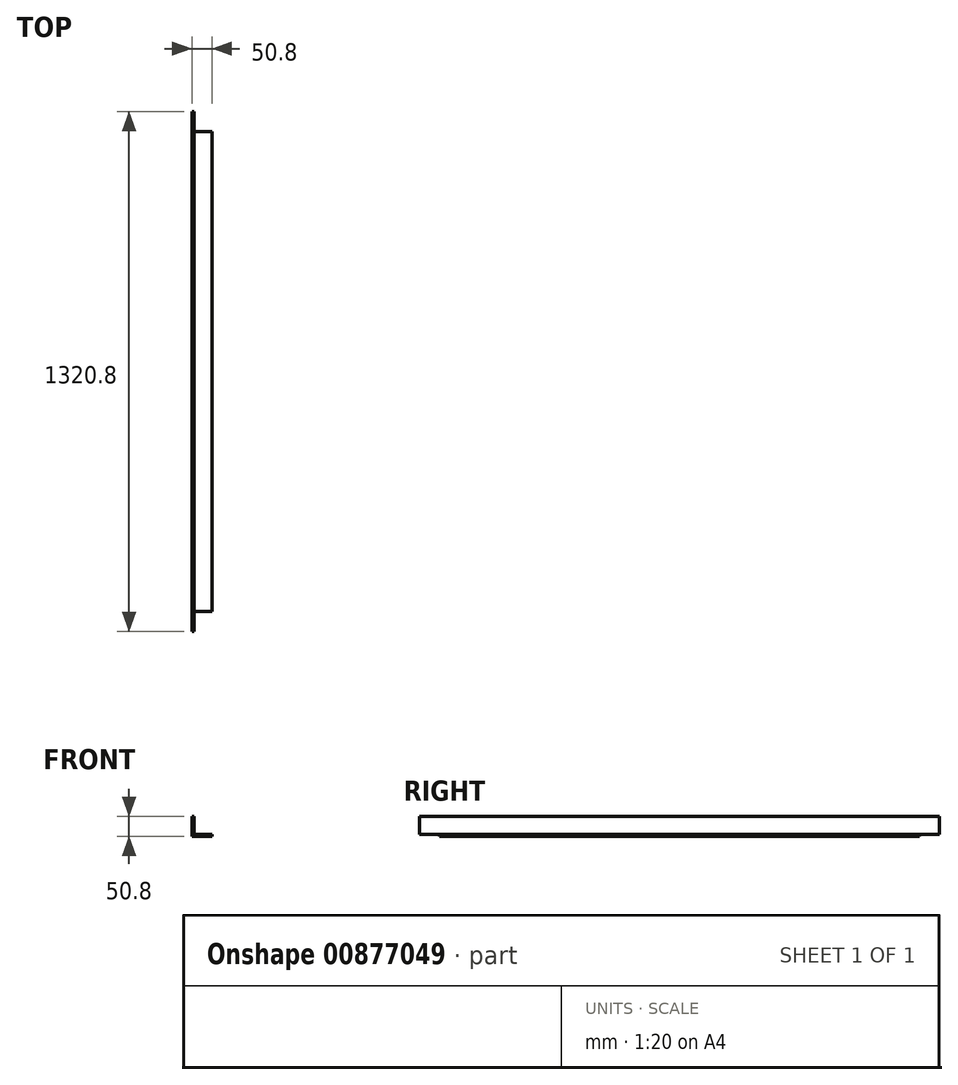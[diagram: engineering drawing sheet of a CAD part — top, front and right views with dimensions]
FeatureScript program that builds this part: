
annotation { "Feature Type Name" : "Feature", "Feature Type Description" : "" }
export const myFeature = defineFeature(function(context is Context, id is Id, definition is map)
    precondition{}
    {
        {
            var Q0;
            Q0=qCreatedBy(makeId("Front.planeOp"),FACE);
            var sketch = newSketch(context, id + "F0", { "sketchPlane" : qUnion([Q0])});
            skLineSegment(sketch, "E0", {"start": v(0, 0) * mm, "end": v(0, 50.8) * mm});
            skLineSegment(sketch, "E1", {"start": v(0, 50.8) * mm, "end": v(4.76, 50.8) * mm});
            skLineSegment(sketch, "E2", {"start": v(4.76, 50.8) * mm, "end": v(4.76, 4.76) * mm});
            skLineSegment(sketch, "E3", {"start": v(4.76, 4.76) * mm, "end": v(50.8, 4.76) * mm});
            skLineSegment(sketch, "E4", {"start": v(50.8, 4.76) * mm, "end": v(50.8, 0) * mm});
            skLineSegment(sketch, "E5", {"start": v(50.8, 0) * mm, "end": v(0, 0) * mm});
            skSolve(sketch);
        }
        {
            var Q0;
            Q0=qSketchRegion(id+"F0",true);
            extrude(context, id + "F1", {"entities" : qUnion([Q0]), "endBound" : BoundingType.SYMMETRIC, "depth" : 1320.8 * mm, "offsetDistance" : 25.4 * mm});
        }
        {
            var Q0;
            Q0=makeQuery(id+"F1.opExtrude","SWEPT_FACE",FACE,{"disambiguationData":[OSD([sQuery(id+"F0.wireOp",EDGE,"E5")])]});
            var sketch = newSketch(context, id + "F2", { "sketchPlane" : qUnion([Q0])});
            skLineSegment(sketch, "E6", {"start": v(50.8, 609.6) * mm, "end": v(50.8, 660.4) * mm});
            skLineSegment(sketch, "E7", {"start": v(50.8, 660.4) * mm, "end": v(0, 660.4) * mm});
            skLineSegment(sketch, "E8", {"start": v(0, 0) * mm, "end": v(50.8, 0) * mm, "construction": true});
            skLineSegment(sketch, "E9", {"start": v(50.8, 609.6) * mm, "end": v(0, 609.6) * mm});
            skLineSegment(sketch, "E10", {"start": v(0, 609.6) * mm, "end": v(0, 660.4) * mm});
            skLineSegment(sketch, "E11.MirrorCS", {"start": v(50.8, -609.6) * mm, "end": v(0, -609.6) * mm});
            skLineSegment(sketch, "E12.MirrorCS", {"start": v(0, -609.6) * mm, "end": v(0, -660.4) * mm});
            skLineSegment(sketch, "E13.MirrorCS", {"start": v(50.8, -660.4) * mm, "end": v(0, -660.4) * mm});
            skLineSegment(sketch, "E14.MirrorCS", {"start": v(50.8, -609.6) * mm, "end": v(50.8, -660.4) * mm});
            skSolve(sketch);
        }
        {
            var Q0;
            Q0=qSketchRegion(id+"F2",true);
            var Q1;
            Q1=makeQuery(id+"F1.opExtrude","SWEPT_FACE",FACE,{"disambiguationData":[OSD([sQuery(id+"F0.wireOp",EDGE,"E3")])]});
            extrude(context, id + "F3", {"entities" : qUnion([Q0]), "operationType" : NewBodyOperationType.REMOVE, "endBound" : BoundingType.UP_TO_SURFACE, "oppositeDirection" : true, "depth" : 25.4 * mm, "endBoundEntityFace" : qUnion([Q1]), "offsetDistance" : 25.4 * mm});
        }
    });
